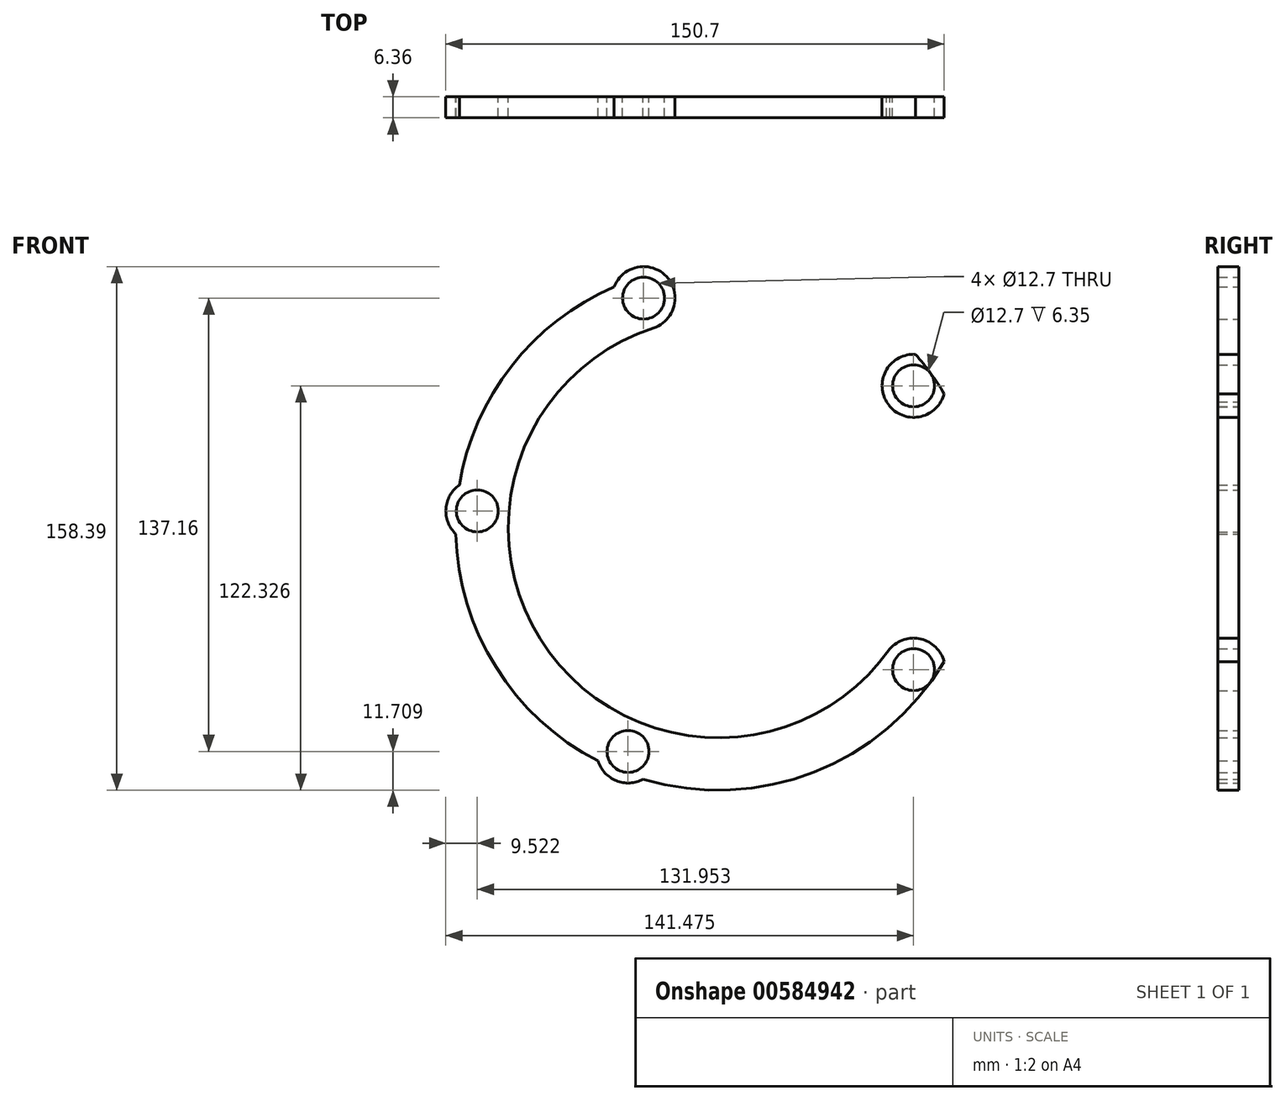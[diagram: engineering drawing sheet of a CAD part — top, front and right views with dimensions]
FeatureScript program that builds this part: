
annotation { "Feature Type Name" : "Feature", "Feature Type Description" : "" }
export const myFeature = defineFeature(function(context is Context, id is Id, definition is map)
    precondition{}
    {
        {
            var Q0;
            Q0=qCreatedBy(makeId("Front.planeOp"),FACE);
            var sketch = newSketch(context, id + "F0", { "sketchPlane" : qUnion([Q0])});
            skCircle(sketch, "E0", {"center": v(59.06, -42.93) * mm, "radius": 6.35 * mm});
            skCircle(sketch, "E1", {"center": v(59.05, 42.93) * mm, "radius": 6.35 * mm});
            skCircle(sketch, "E2", {"center": v(-22.6, 69.47) * mm, "radius": 6.35 * mm});
            skCircle(sketch, "E3", {"center": v(-72.9, 5.08) * mm, "radius": 6.35 * mm});
            skCircle(sketch, "E4", {"center": v(-27.3, -67.7) * mm, "radius": 6.35 * mm});
            skCircle(sketch, "E5", {"center": v(0, 0) * mm, "radius": 63.53 * mm});
            skCircle(sketch, "E6", {"center": v(0, 0) * mm, "radius": 79.4 * mm});
            skCircle(sketch, "E7", {"center": v(59.05, 42.93) * mm, "radius": 9.53 * mm});
            skCircle(sketch, "E8", {"center": v(-22.6, 69.47) * mm, "radius": 9.53 * mm});
            skCircle(sketch, "E9", {"center": v(-72.9, 5.08) * mm, "radius": 9.53 * mm});
            skCircle(sketch, "E10", {"center": v(-27.3, -67.7) * mm, "radius": 9.53 * mm});
            skCircle(sketch, "E11", {"center": v(59.06, -42.93) * mm, "radius": 9.53 * mm});
            skSolve(sketch);
        }
        {
            var Q0;
            {var subQ0=sQuery(id+"F0.wireOp",EDGE,"E8");var subQ3=sQuery(id+"F0.wireOp",EDGE,"E5");var subQ4=makeQuery(id+"F0.imprint","INTERSECT",VERTEX,{"derivedFrom":[subQ3,subQ0]});Q0=makeQuery(id+"F0.imprint","IMPRINT",FACE,{"disambiguationData":[TD([[makeQuery(id+"F0.imprint","IMPRINT",EDGE,{"disambiguationData":[TD([[subQ4,-1.0]])],"derivedFrom":subQ3}),-1.0]])]});}
            var Q1;
            {var subQ0=sQuery(id+"F0.wireOp",EDGE,"E6");var subQ1=sQuery(id+"F0.wireOp",EDGE,"E3");var subQ2=makeQuery(id+"F0.imprint","INTERSECT",VERTEX,{"disambiguationData":[OD(0.0)],"derivedFrom":[subQ1,subQ0]});Q1=makeQuery(id+"F0.imprint","IMPRINT",FACE,{"disambiguationData":[TD([[makeQuery(id+"F0.imprint","IMPRINT",EDGE,{"disambiguationData":[TD([[subQ2,-1.0]])],"derivedFrom":subQ1}),-1.0]])]});}
            var Q2;
            {var subQ0=sQuery(id+"F0.wireOp",EDGE,"E6");var subQ1=sQuery(id+"F0.wireOp",EDGE,"E3");var subQ2=makeQuery(id+"F0.imprint","INTERSECT",VERTEX,{"disambiguationData":[OD(0.0)],"derivedFrom":[subQ1,subQ0]});Q2=makeQuery(id+"F0.imprint","IMPRINT",FACE,{"disambiguationData":[TD([[makeQuery(id+"F0.imprint","IMPRINT",EDGE,{"disambiguationData":[TD([[subQ2,1.0]])],"derivedFrom":subQ1}),-1.0]])]});}
            var Q3;
            Q3=makeQuery(id+"F0.imprint","IMPRINT",FACE,{"disambiguationData":[TD([[makeQuery(id+"F0.imprint","IMPRINT",EDGE,{"derivedFrom":sQuery(id+"F0.wireOp",EDGE,"E4")}),-1.0]])]});
            var Q4;
            {var subQ0=sQuery(id+"F0.wireOp",EDGE,"E10");var subQ1=sQuery(id+"F0.wireOp",EDGE,"E6");var subQ2=makeQuery(id+"F0.imprint","INTERSECT",VERTEX,{"disambiguationData":[OD(0.0)],"derivedFrom":[subQ1,subQ0]});Q4=makeQuery(id+"F0.imprint","IMPRINT",FACE,{"disambiguationData":[TD([[makeQuery(id+"F0.imprint","IMPRINT",EDGE,{"disambiguationData":[TD([[subQ2,-1.0]])],"derivedFrom":subQ1}),-1.0]])]});}
            var Q5;
            {var subQ0=sQuery(id+"F0.wireOp",EDGE,"E10");var subQ1=sQuery(id+"F0.wireOp",EDGE,"E5");var subQ2=makeQuery(id+"F0.imprint","INTERSECT",VERTEX,{"disambiguationData":[OD(1.0)],"derivedFrom":[subQ1,subQ0]});Q5=makeQuery(id+"F0.imprint","IMPRINT",FACE,{"disambiguationData":[TD([[makeQuery(id+"F0.imprint","IMPRINT",EDGE,{"disambiguationData":[TD([[subQ2,-1.0]])],"derivedFrom":subQ1}),-1.0]])]});}
            var Q6;
            Q6=makeQuery(id+"F0.imprint","IMPRINT",FACE,{"disambiguationData":[TD([[makeQuery(id+"F0.imprint","IMPRINT",EDGE,{"derivedFrom":sQuery(id+"F0.wireOp",EDGE,"E0")}),-1.0]])]});
            var Q7;
            {var subQ0=sQuery(id+"F0.wireOp",EDGE,"E7");var subQ1=sQuery(id+"F0.wireOp",EDGE,"E5");var subQ2=makeQuery(id+"F0.imprint","INTERSECT",VERTEX,{"disambiguationData":[OD(1.0)],"derivedFrom":[subQ1,subQ0]});Q7=makeQuery(id+"F0.imprint","IMPRINT",FACE,{"disambiguationData":[TD([[makeQuery(id+"F0.imprint","IMPRINT",EDGE,{"disambiguationData":[TD([[subQ2,1.0]])],"derivedFrom":subQ1}),-1.0]])]});}
            var Q8;
            {var subQ0=sQuery(id+"F0.wireOp",EDGE,"E7");var subQ1=sQuery(id+"F0.wireOp",EDGE,"E5");var subQ2=makeQuery(id+"F0.imprint","INTERSECT",VERTEX,{"disambiguationData":[OD(0.0)],"derivedFrom":[subQ1,subQ0]});Q8=makeQuery(id+"F0.imprint","IMPRINT",FACE,{"disambiguationData":[TD([[makeQuery(id+"F0.imprint","IMPRINT",EDGE,{"disambiguationData":[TD([[subQ2,-1.0]])],"derivedFrom":subQ1}),-1.0]])]});}
            var Q9;
            {var subQ4=sQuery(id+"F0.wireOp",EDGE,"E2");Q9=makeQuery(id+"F0.imprint","IMPRINT",FACE,{"disambiguationData":[TD([[makeQuery(id+"F0.imprint","IMPRINT",EDGE,{"derivedFrom":subQ4}),-1.0]])]});}
            var Q10;
            {var subQ0=sQuery(id+"F0.wireOp",EDGE,"E6");var subQ1=makeQuery(id+"F0.imprint","INTERSECT",VERTEX,{"derivedFrom":[sQuery(id+"F0.wireOp",EDGE,"E2"),subQ0]});Q10=makeQuery(id+"F0.imprint","IMPRINT",FACE,{"disambiguationData":[TD([[makeQuery(id+"F0.imprint","IMPRINT",EDGE,{"disambiguationData":[TD([[subQ1,1.0]])],"derivedFrom":subQ0}),-1.0]])]});}
            var Q11;
            {var subQ0=sQuery(id+"F0.wireOp",EDGE,"E7");var subQ1=sQuery(id+"F0.wireOp",EDGE,"E6");var subQ2=makeQuery(id+"F0.imprint","INTERSECT",VERTEX,{"disambiguationData":[OD(0.0)],"derivedFrom":[subQ1,subQ0]});Q11=makeQuery(id+"F0.imprint","IMPRINT",FACE,{"disambiguationData":[TD([[makeQuery(id+"F0.imprint","IMPRINT",EDGE,{"disambiguationData":[TD([[subQ2,1.0]])],"derivedFrom":subQ1}),-1.0]])]});}
            var Q12;
            Q12=makeQuery(id+"F0.imprint","IMPRINT",FACE,{"disambiguationData":[TD([[makeQuery(id+"F0.imprint","IMPRINT",EDGE,{"derivedFrom":sQuery(id+"F0.wireOp",EDGE,"E1")}),-1.0]])]});
            var Q13;
            {var subQ0=sQuery(id+"F0.wireOp",EDGE,"E11");var subQ1=sQuery(id+"F0.wireOp",EDGE,"E6");var subQ2=makeQuery(id+"F0.imprint","INTERSECT",VERTEX,{"disambiguationData":[OD(0.0)],"derivedFrom":[subQ1,subQ0]});Q13=makeQuery(id+"F0.imprint","IMPRINT",FACE,{"disambiguationData":[TD([[makeQuery(id+"F0.imprint","IMPRINT",EDGE,{"disambiguationData":[TD([[subQ2,-1.0]])],"derivedFrom":subQ1}),-1.0]])]});}
            extrude(context, id + "F1", {"entities" : qUnion([Q0, Q1, Q2, Q3, Q4, Q5, Q6, Q7, Q8, Q9, Q10, Q11, Q12, Q13]), "endBound" : BoundingType.SYMMETRIC, "depth" : 6.35 * mm, "offsetDistance" : 25.4 * mm});
        }
    });
